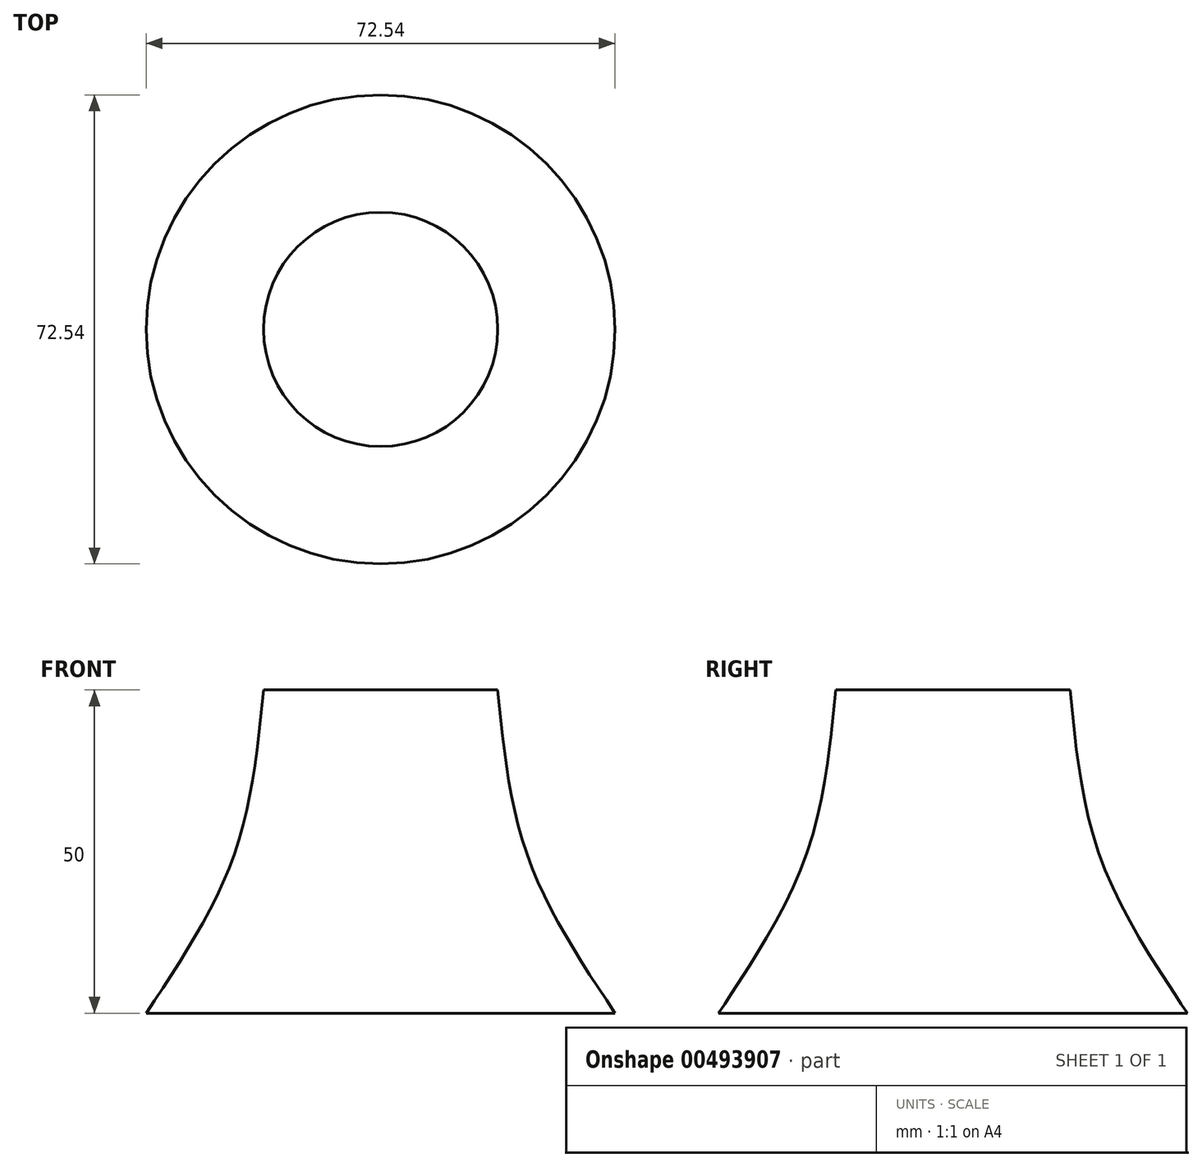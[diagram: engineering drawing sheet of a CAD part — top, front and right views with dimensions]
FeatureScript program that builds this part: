
annotation { "Feature Type Name" : "Feature", "Feature Type Description" : "" }
export const myFeature = defineFeature(function(context is Context, id is Id, definition is map)
    precondition{}
    {
        {
            var Q0;
            Q0=qCreatedBy(makeId("Top.planeOp"),FACE);
            cPlane(context, id + "F0", {"entities" : qUnion([Q0]), "cplaneType" : CPlaneType.OFFSET, "offset" : 25 * mm, "width" : 150 * mm, "height" : 150 * mm});
        }
        {
            var Q0;
            Q0=qCreatedBy(makeId("Top.planeOp"),FACE);
            cPlane(context, id + "F1", {"entities" : qUnion([Q0]), "cplaneType" : CPlaneType.OFFSET, "offset" : 25 * mm, "oppositeDirection" : true, "width" : 150 * mm, "height" : 150 * mm});
        }
        {
            var Q0;
            Q0=qCreatedBy(makeId("Top.planeOp"),FACE);
            var sketch = newSketch(context, id + "F2", { "sketchPlane" : qUnion([Q0])});
            skCircle(sketch, "E0", {"center": v(0, 0) * mm, "radius": 22.5 * mm});
            skSolve(sketch);
        }
        {
            var Q0;
            Q0=qCreatedBy(id+"F0.planeOp",FACE);
            var sketch = newSketch(context, id + "F3", { "sketchPlane" : qUnion([Q0])});
            skCircle(sketch, "E1", {"center": v(0, 0) * mm, "radius": 18.12 * mm});
            skSolve(sketch);
        }
        {
            var Q0;
            Q0=qCreatedBy(id+"F1.planeOp",FACE);
            var sketch = newSketch(context, id + "F4", { "sketchPlane" : qUnion([Q0])});
            skCircle(sketch, "E2", {"center": v(0, 0) * mm, "radius": 36.27 * mm});
            skSolve(sketch);
        }
        {
            var Q0;
            Q0=makeQuery(id+"F4.imprint","IMPRINT",FACE,{"disambiguationData":[TD([[makeQuery(id+"F4.imprint","IMPRINT",EDGE,{"derivedFrom":sQuery(id+"F4.wireOp",EDGE,"E2")}),1.0]])]});
            var Q1;
            Q1=makeQuery(id+"F2.imprint","IMPRINT",FACE,{"disambiguationData":[TD([[makeQuery(id+"F2.imprint","IMPRINT",EDGE,{"derivedFrom":sQuery(id+"F2.wireOp",EDGE,"E0")}),1.0]])]});
            var Q2;
            Q2=makeQuery(id+"F3.imprint","IMPRINT",FACE,{"disambiguationData":[TD([[makeQuery(id+"F3.imprint","IMPRINT",EDGE,{"derivedFrom":sQuery(id+"F3.wireOp",EDGE,"E1")}),1.0]])]});
            loft(context, id + "F5", {"sheetProfilesArray" : [{ "sheetProfileEntities" : qUnion([Q0]) }, { "sheetProfileEntities" : qUnion([Q1]) }, { "sheetProfileEntities" : qUnion([Q2]) }]});
        }
    });
